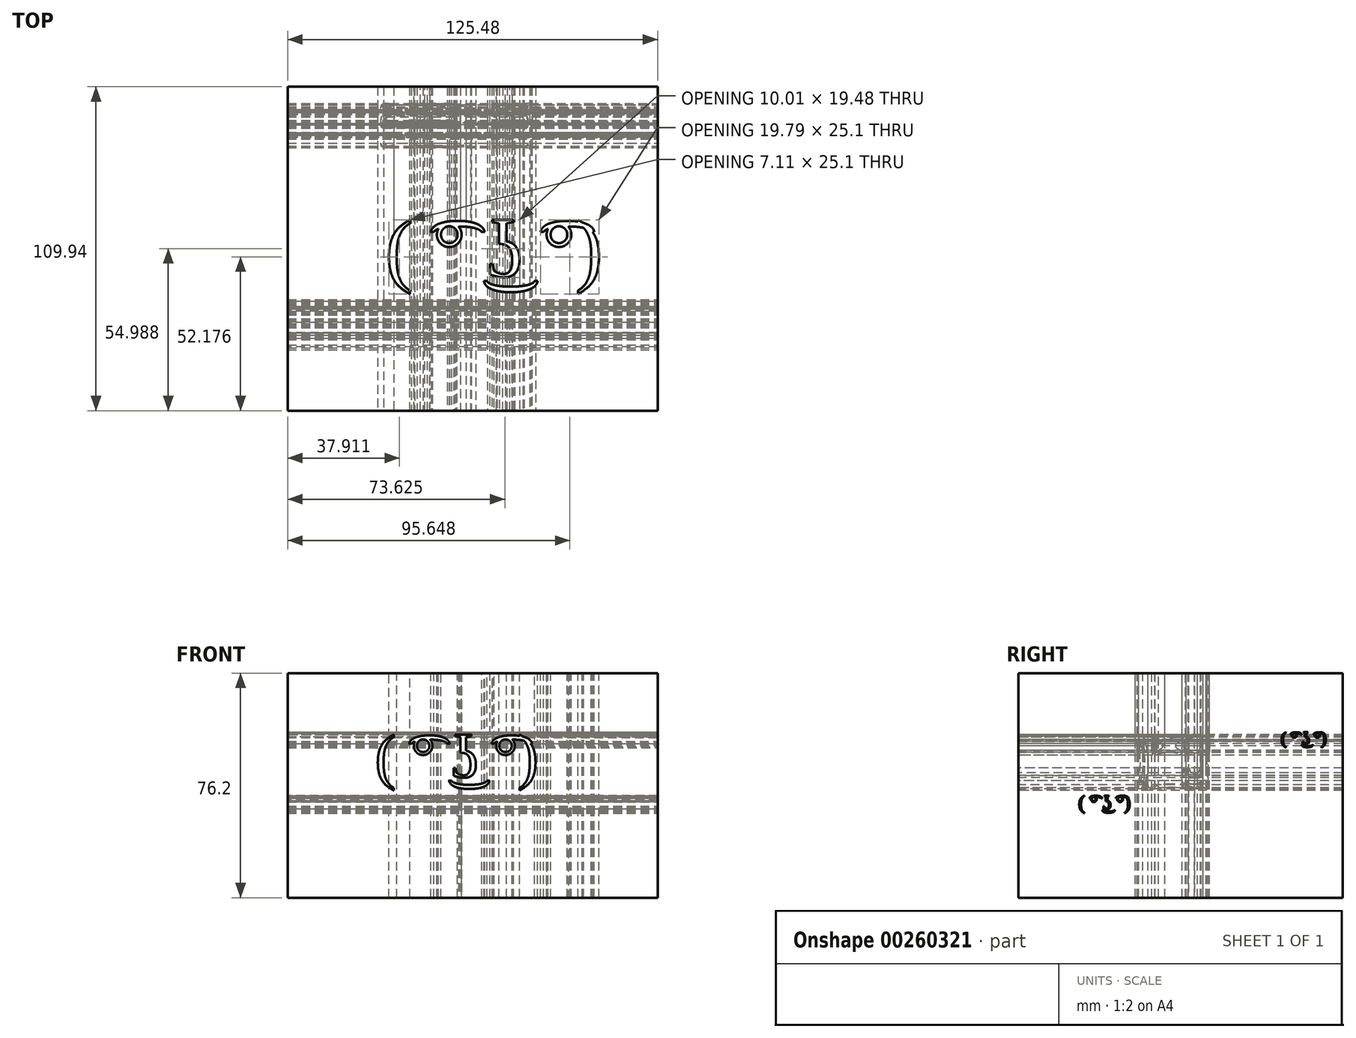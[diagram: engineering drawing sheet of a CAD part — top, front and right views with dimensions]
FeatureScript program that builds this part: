
annotation { "Feature Type Name" : "Feature", "Feature Type Description" : "" }
export const myFeature = defineFeature(function(context is Context, id is Id, definition is map)
    precondition{}
    {
        {
            var Q0;
            Q0=qCreatedBy(makeId("Top.planeOp"),FACE);
            var sketch = newSketch(context, id + "F0", { "sketchPlane" : qUnion([Q0])});
            skLineSegment(sketch, "E0.bottom", {"start": v(-62.74, 54.97) * mm, "end": v(62.74, 54.97) * mm});
            skLineSegment(sketch, "E0.top", {"start": v(-62.74, -54.97) * mm, "end": v(62.74, -54.97) * mm});
            skLineSegment(sketch, "E0.left", {"start": v(-62.74, 54.97) * mm, "end": v(-62.74, -54.97) * mm});
            skLineSegment(sketch, "E0.right", {"start": v(62.74, 54.97) * mm, "end": v(62.74, -54.97) * mm});
            skPoint(sketch, "E0.middle", {"position": v(0, 0) * mm});
            skSolve(sketch);
        }
        {
            var Q0;
            Q0 = qSketchRegion(id + "F0", true);
            extrude(context, id + "F1", {"entities" : qUnion([Q0]), "depth" : 76.2 * mm});
        }
        {
            var Q0;
            Q0=makeQuery(id+"F1.opExtrude","CAP_FACE",FACE,{"disambiguationData":[OSD([sQuery(id+"F0.wireOp",EDGE,"E0.bottom"),sQuery(id+"F0.wireOp",EDGE,"E0.top"),sQuery(id+"F0.wireOp",EDGE,"E0.left"),sQuery(id+"F0.wireOp",EDGE,"E0.right")])],"isStart":false});
            var sketch = newSketch(context, id + "F2", { "sketchPlane" : qUnion([Q0])});
            skText(sketch, "E1", { "text": " ( ͡° ͜ʖ ͡°) ", "fontName": "Tinos-Regular.ttf"});
            const initialGuessF2  = {"E1": [-0.03652, -0.00945, 1, 0, 0.01993]};
            skSetInitialGuess(sketch, initialGuessF2);
            skSolve(sketch);
        }
        {
            var Q0;
            Q0 = qSketchRegion(id + "F2", true);
            extrude(context, id + "F3", {"entities" : qUnion([Q0]), "operationType" : NewBodyOperationType.REMOVE, "oppositeDirection" : true, "depth" : 152.4 * mm});
        }
        {
            var Q0;
            Q0=makeQuery(id+"F1.opExtrude","SWEPT_FACE",FACE,{"disambiguationData":[OSD([sQuery(id+"F0.wireOp",EDGE,"E0.top")])]});
            var sketch = newSketch(context, id + "F4", { "sketchPlane" : qUnion([Q0])});
            skText(sketch, "E2", { "text": " ( ͡° ͜ʖ ͡°) ", "fontName": "Tinos-Regular.ttf"});
            const initialGuessF4  = {"E2": [-0.03828, 0.04087, 1, 0, 0.01497]};
            skSetInitialGuess(sketch, initialGuessF4);
            skSolve(sketch);
        }
        {
            var Q0;
            Q0 = qSketchRegion(id + "F4", true);
            extrude(context, id + "F5", {"entities" : qUnion([Q0]), "operationType" : NewBodyOperationType.REMOVE, "oppositeDirection" : true, "depth" : 152.4 * mm});
        }
        {
            var Q0;
            Q0=makeQuery(id+"F1.opExtrude","SWEPT_FACE",FACE,{"disambiguationData":[OSD([sQuery(id+"F0.wireOp",EDGE,"E0.right")])]});
            var sketch = newSketch(context, id + "F6", { "sketchPlane" : qUnion([Q0])});
            skText(sketch, "E3", { "text": " ( ͡° ͜ʖ ͡°) ", "fontName": "Tinos-Regular.ttf"});
            const initialGuessF6  = {"E3": [-0.03629, 0.03006, 1, 0, 0.00479]};
            skSetInitialGuess(sketch, initialGuessF6);
            skSolve(sketch);
        }
        {
            var Q0;
            Q0 = qSketchRegion(id + "F6", true);
            extrude(context, id + "F7", {"entities" : qUnion([Q0]), "operationType" : NewBodyOperationType.REMOVE, "oppositeDirection" : true, "depth" : 177.8 * mm});
        }
        {
            var Q0;
            {var subQ0=sQuery(id+"F0.wireOp",EDGE,"E0.right");var subQ3=sQuery(id+"F0.wireOp",EDGE,"E0.bottom");Q0=makeQuery(id+"F7.boolean.opBoolean","SPLIT",FACE,{"disambiguationData":[TD([makeQuery(id+"F1.opExtrude","SWEPT_FACE",FACE,{"disambiguationData":[OSD([subQ3])]})])],"derivedFrom":makeQuery(id+"F1.opExtrude","SWEPT_FACE",FACE,{"disambiguationData":[OSD([subQ0])]})});}
            var sketch = newSketch(context, id + "F8", { "sketchPlane" : qUnion([Q0])});
            skText(sketch, "E4", { "text": " ( ͡° ͜ʖ ͡°) ", "fontName": "Tinos-Regular.ttf"});
            const initialGuessF8  = {"E4": [0.03255, 0.05215, 1, 0, 0.0042]};
            skSetInitialGuess(sketch, initialGuessF8);
            skSolve(sketch);
        }
        {
            var Q0;
            Q0 = qSketchRegion(id + "F8", true);
            extrude(context, id + "F9", {"entities" : qUnion([Q0]), "operationType" : NewBodyOperationType.REMOVE, "oppositeDirection" : true, "depth" : 177.8 * mm});
        }
    });
